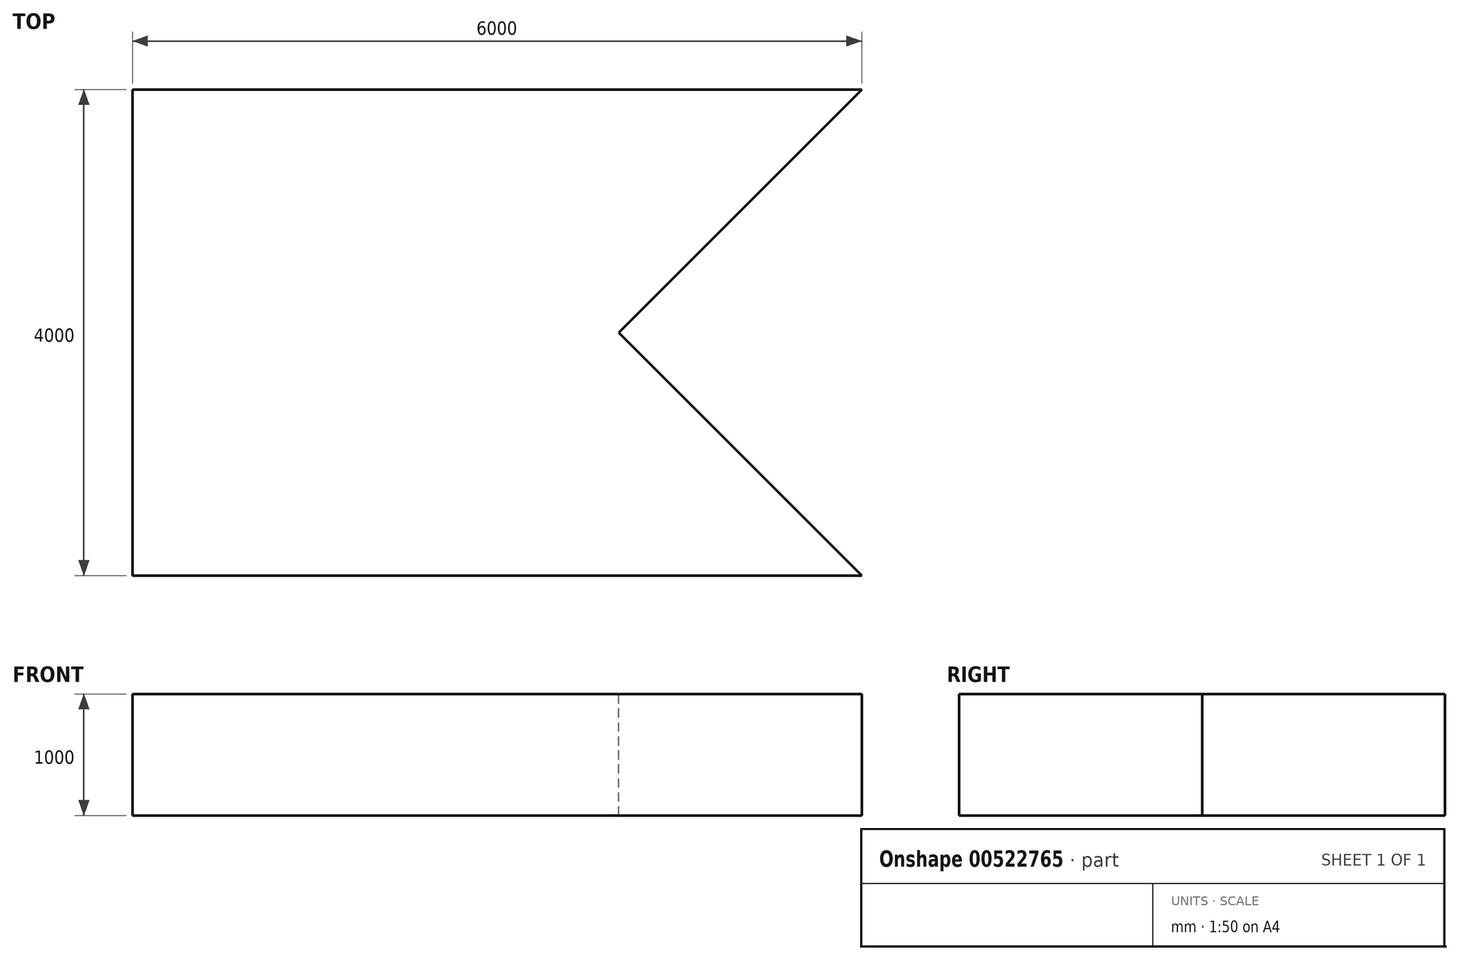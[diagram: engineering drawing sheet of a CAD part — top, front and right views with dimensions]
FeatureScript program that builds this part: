
annotation { "Feature Type Name" : "Feature", "Feature Type Description" : "" }
export const myFeature = defineFeature(function(context is Context, id is Id, definition is map)
    precondition{}
    {
        {
            var Q0;
            Q0=qCreatedBy(makeId("Top.planeOp"),FACE);
            var sketch = newSketch(context, id + "F0", { "sketchPlane" : qUnion([Q0])});
            skLineSegment(sketch, "E0", {"start": v(0, 0) * mm, "end": v(0, 4000) * mm});
            skLineSegment(sketch, "E1", {"start": v(0, 4000) * mm, "end": v(6000, 4000) * mm});
            skLineSegment(sketch, "E2", {"start": v(6000, 4000) * mm, "end": v(4000, 2000) * mm});
            skLineSegment(sketch, "E3", {"start": v(0, 0) * mm, "end": v(6000, 0) * mm});
            skLineSegment(sketch, "E4", {"start": v(6000, 0) * mm, "end": v(4000, 2000) * mm});
            skSolve(sketch);
        }
        {
            var Q0;
            Q0=makeQuery(id+"F0.imprint","IMPRINT",FACE,{"disambiguationData":[TD([[makeQuery(id+"F0.imprint","IMPRINT",EDGE,{"derivedFrom":sQuery(id+"F0.wireOp",EDGE,"E0")}),-1.0]])]});
            extrude(context, id + "F1", {"entities" : qUnion([Q0]), "oppositeDirection" : true, "depth" : 1000 * mm, "offsetDistance" : 25 * mm});
        }
    });
